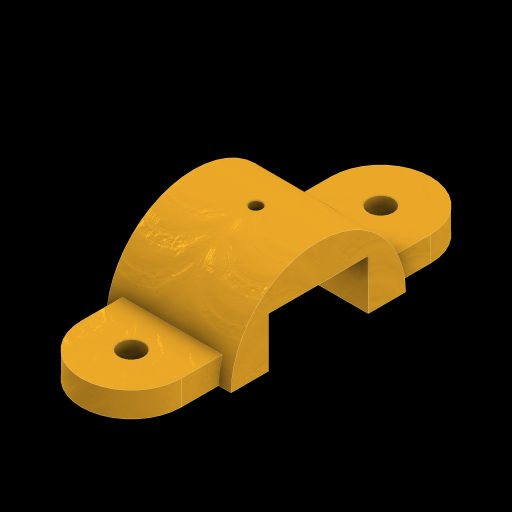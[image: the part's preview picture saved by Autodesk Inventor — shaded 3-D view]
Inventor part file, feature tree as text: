
AUTODESK INVENTOR PART (.ipt)
format: ipt  version: 2024 (Build 280153000, 153)  size: 212,992 bytes
history: native  units: in
note: dims shown in document units (in); Inventor stores cm internally (conversion verified against a paired STEP export)
features: extrude x6, sketch x5
ambient origin geometry x8: Origin, YZ Plane, XZ Plane, XY Plane, X Axis, Y Axis, Z Axis, Center Point
bodies: Solid1 (feature_tree)
feature tree (11):
  extrude  "BASE"  Depth=0.5in
  sketch  "Sketch2"  dims[d2=0.5in d3=1.0in]
  extrude  "REMOVED CENTER OF BASE"  Depth=1.0in
  extrude  "ARCH"  Depth=1.75in
  extrude  "TOPHOLE"  TaperAngle=0.0deg  [1 undecoded]
  extrude  "CIRCULAR"  Depth=0.25in
  extrude  "SQUARE"  TaperAngle=0.0deg  [1 undecoded]
  sketch  "Sketch1"  dims[d0=5.0in d1=0.5in]
  sketch  "Sketch3"  dims[d5=0.5in d6=0.0in d7=1.75in]
  sketch  "Sketch5"  dims[d8=1.25in d9=0.0in d10=0.0in]
  sketch  "Sketch6"  dims[d11=2.5in d12=0.0in d13=0.25in d14=0.0in d15=0.0in d16=2.5in d17=1.25in d18=0.625in d19=0.0in d20=0.0in d21=2.5in d22=0.0in d23=2.0in d24=1.0in d25=1.0in]
note: 2 required parameter values undecoded (feature->parameter linkage not recoverable at this tier; creation-order binding heuristic only, values carry confidence <= 0.55)
